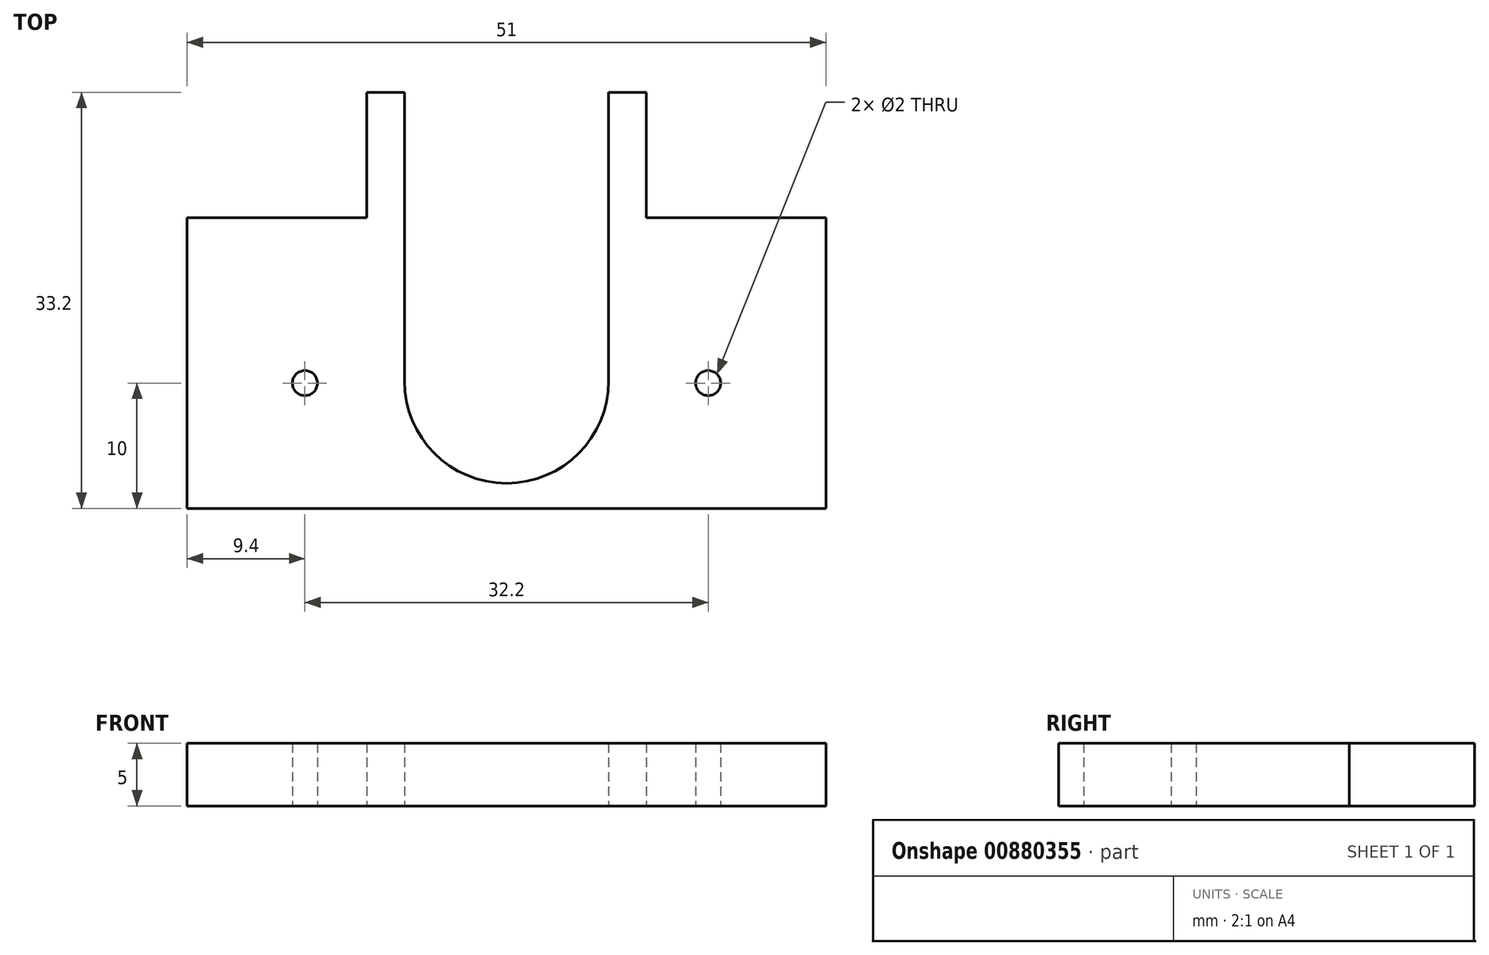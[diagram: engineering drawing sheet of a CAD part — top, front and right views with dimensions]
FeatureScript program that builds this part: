
annotation { "Feature Type Name" : "Feature", "Feature Type Description" : "" }
export const myFeature = defineFeature(function(context is Context, id is Id, definition is map)
    precondition{}
    {
        {
            var Q0;
            Q0=qCreatedBy(makeId("Top.planeOp"),FACE);
            var sketch = newSketch(context, id + "F0", { "sketchPlane" : qUnion([Q0])});
            skLineSegment(sketch, "E0.bottom", {"start": v(-25.5, 13.05) * mm, "end": v(-11.15, 13.05) * mm});
            skLineSegment(sketch, "E0.top", {"start": v(-25.5, -10.15) * mm, "end": v(25.5, -10.15) * mm});
            skLineSegment(sketch, "E0.left", {"start": v(-25.5, 13.05) * mm, "end": v(-25.5, -10.15) * mm});
            skLineSegment(sketch, "E0.right", {"start": v(25.5, 13.05) * mm, "end": v(25.5, -10.15) * mm});
            skArc(sketch, "E1", {"start": v(-8.15, 0) * mm, "mid": v(0, -8.15) * mm, "end": v(8.15, 0) * mm});
            skLineSegment(sketch, "E2", {"start": v(11.15, 13.05) * mm, "end": v(25.5, 13.05) * mm});
            skLineSegment(sketch, "E3", {"start": v(-11.15, 13.05) * mm, "end": v(-11.15, 23.05) * mm});
            skLineSegment(sketch, "E4", {"start": v(11.15, 13.05) * mm, "end": v(11.15, 23.05) * mm});
            skLineSegment(sketch, "E5", {"start": v(-11.15, 23.05) * mm, "end": v(-8.15, 23.05) * mm});
            skLineSegment(sketch, "E6", {"start": v(-8.15, 23.05) * mm, "end": v(-8.15, 0) * mm});
            skLineSegment(sketch, "E7", {"start": v(8.15, 0) * mm, "end": v(8.15, 23.05) * mm});
            skLineSegment(sketch, "E8", {"start": v(8.15, 23.05) * mm, "end": v(11.15, 23.05) * mm});
            skCircle(sketch, "E9", {"center": v(-16.1, -0.15) * mm, "radius": 1 * mm});
            skCircle(sketch, "E10", {"center": v(16.1, -0.15) * mm, "radius": 1 * mm});
            skSolve(sketch);
        }
        {
            var Q0;
            Q0=makeQuery(id+"F0.imprint","IMPRINT",FACE,{"disambiguationData":[TD([[makeQuery(id+"F0.imprint","IMPRINT",EDGE,{"derivedFrom":sQuery(id+"F0.wireOp",EDGE,"E0.bottom")}),-1.0]])]});
            extrude(context, id + "F1", {"entities" : qUnion([Q0]), "depth" : 5 * mm, "offsetDistance" : 25 * mm});
        }
    });
